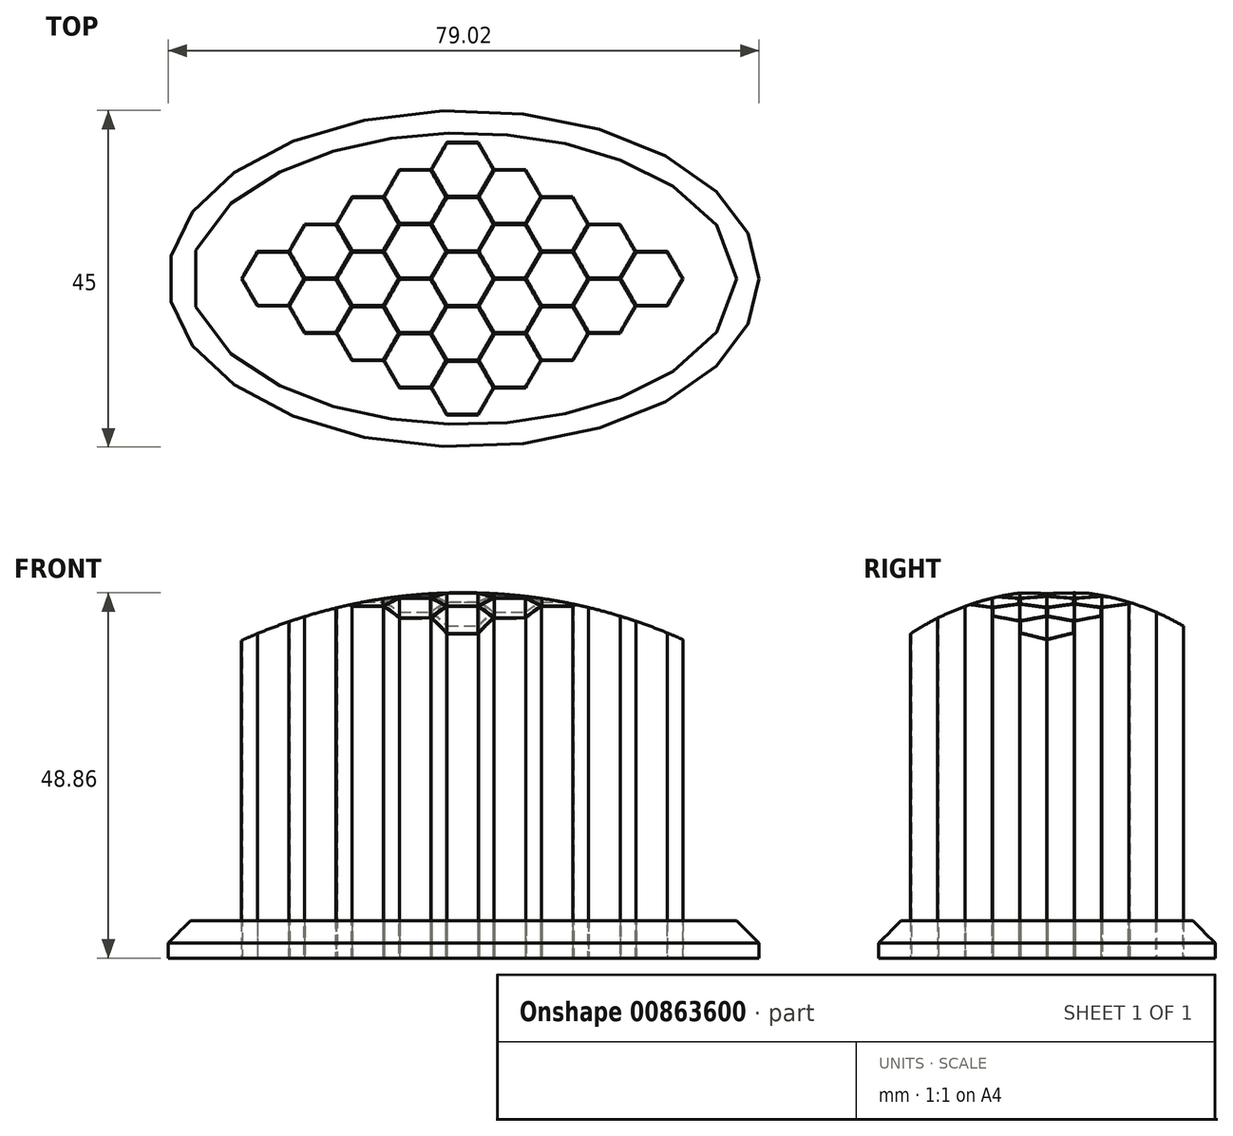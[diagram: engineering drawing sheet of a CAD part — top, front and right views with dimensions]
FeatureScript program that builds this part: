
annotation { "Feature Type Name" : "Feature", "Feature Type Description" : "" }
export const myFeature = defineFeature(function(context is Context, id is Id, definition is map)
    precondition{}
    {
        {
            var Q0;
            Q0=qCreatedBy(makeId("Top.planeOp"),FACE);
            var sketch = newSketch(context, id + "F0", { "sketchPlane" : qUnion([Q0])});
            skCircle(sketch, "E0.cCircle", {"center": v(0, 0) * mm, "radius": 3.55 * mm, "construction": true});
            skLineSegment(sketch, "E0.0", {"start": v(4.1, 0) * mm, "end": v(2.05, -3.55) * mm});
            skLineSegment(sketch, "E0.1", {"start": v(2.05, -3.55) * mm, "end": v(-2.05, -3.55) * mm});
            skLineSegment(sketch, "E0.2", {"start": v(-2.05, -3.55) * mm, "end": v(-4.1, 0) * mm});
            skLineSegment(sketch, "E0.3", {"start": v(-4.1, 0) * mm, "end": v(-2.05, 3.55) * mm});
            skLineSegment(sketch, "E0.4", {"start": v(-2.05, 3.55) * mm, "end": v(2.05, 3.55) * mm});
            skLineSegment(sketch, "E0.5", {"start": v(2.05, 3.55) * mm, "end": v(4.1, 0) * mm});
            skPoint(sketch, "E0.0.midPoint", {"position": v(3.07, -1.78) * mm});
            skCircle(sketch, "E1.cCircle", {"center": v(0, 0) * mm, "radius": 3.65 * mm, "construction": true});
            skLineSegment(sketch, "E1.0", {"start": v(4.21, 0) * mm, "end": v(2.1, -3.65) * mm});
            skLineSegment(sketch, "E1.1", {"start": v(2.1, -3.65) * mm, "end": v(-2.1, -3.65) * mm});
            skLineSegment(sketch, "E1.2", {"start": v(-2.1, -3.65) * mm, "end": v(-4.21, 0) * mm});
            skLineSegment(sketch, "E1.3", {"start": v(-4.21, 0) * mm, "end": v(-2.1, 3.65) * mm});
            skLineSegment(sketch, "E1.4", {"start": v(-2.1, 3.65) * mm, "end": v(2.1, 3.65) * mm});
            skLineSegment(sketch, "E1.5", {"start": v(2.1, 3.65) * mm, "end": v(4.21, 0) * mm});
            skPoint(sketch, "E1.0.midPoint", {"position": v(3.16, -1.82) * mm});
            skSolve(sketch);
        }
        {
            var Q0;
            Q0 = qSketchRegion(id + "F0", true);
            extrude(context, id + "F1", {"entities" : qUnion([Q0]), "depth" : 50 * mm, "offsetDistance" : 25 * mm});
        }
        {
            var Q0;
            Q0=makeQuery(id+"F1.opExtrude","SWEPT_BODY",BODY,{"disambiguationData":[OSD([sQuery(id+"F0.wireOp",EDGE,"E0.0"),sQuery(id+"F0.wireOp",EDGE,"E0.1"),sQuery(id+"F0.wireOp",EDGE,"E0.2"),sQuery(id+"F0.wireOp",EDGE,"E0.3"),sQuery(id+"F0.wireOp",EDGE,"E0.4"),sQuery(id+"F0.wireOp",EDGE,"E0.5"),sQuery(id+"F0.wireOp",EDGE,"E1.0"),sQuery(id+"F0.wireOp",EDGE,"E1.1"),sQuery(id+"F0.wireOp",EDGE,"E1.2"),sQuery(id+"F0.wireOp",EDGE,"E1.3"),sQuery(id+"F0.wireOp",EDGE,"E1.4"),sQuery(id+"F0.wireOp",EDGE,"E1.5")])]});
            transform(context, id + "F2", {"entities" : qUnion([Q0]), "transformType" : TransformType.TRANSLATION_3D, "dx" : 6.32 * mm, "dy" : -3.65 * mm, "dz" : 0 * mm, "makeCopy" : true});
        }
        {
            var Q0;
            Q0=makeQuery(id+"F2.opPattern","COPY",BODY,{"derivedFrom":makeQuery(id+"F1.opExtrude","SWEPT_BODY",BODY,{"disambiguationData":[OSD([sQuery(id+"F0.wireOp",EDGE,"E0.0"),sQuery(id+"F0.wireOp",EDGE,"E0.1"),sQuery(id+"F0.wireOp",EDGE,"E0.2"),sQuery(id+"F0.wireOp",EDGE,"E0.3"),sQuery(id+"F0.wireOp",EDGE,"E0.4"),sQuery(id+"F0.wireOp",EDGE,"E0.5"),sQuery(id+"F0.wireOp",EDGE,"E1.0"),sQuery(id+"F0.wireOp",EDGE,"E1.1"),sQuery(id+"F0.wireOp",EDGE,"E1.2"),sQuery(id+"F0.wireOp",EDGE,"E1.3"),sQuery(id+"F0.wireOp",EDGE,"E1.4"),sQuery(id+"F0.wireOp",EDGE,"E1.5")])]}),"instanceName":"1"});
            transform(context, id + "F3", {"entities" : qUnion([Q0]), "transformType" : TransformType.TRANSLATION_3D, "dx" : 0 * mm, "dy" : 7.3 * mm, "dz" : 0 * mm, "makeCopy" : true});
        }
        {
            var Q0;
            Q0=makeQuery(id+"F1.opExtrude","SWEPT_BODY",BODY,{"disambiguationData":[OSD([sQuery(id+"F0.wireOp",EDGE,"E0.0"),sQuery(id+"F0.wireOp",EDGE,"E0.1"),sQuery(id+"F0.wireOp",EDGE,"E0.2"),sQuery(id+"F0.wireOp",EDGE,"E0.3"),sQuery(id+"F0.wireOp",EDGE,"E0.4"),sQuery(id+"F0.wireOp",EDGE,"E0.5"),sQuery(id+"F0.wireOp",EDGE,"E1.0"),sQuery(id+"F0.wireOp",EDGE,"E1.1"),sQuery(id+"F0.wireOp",EDGE,"E1.2"),sQuery(id+"F0.wireOp",EDGE,"E1.3"),sQuery(id+"F0.wireOp",EDGE,"E1.4"),sQuery(id+"F0.wireOp",EDGE,"E1.5")])]});
            transform(context, id + "F4", {"entities" : qUnion([Q0]), "transformType" : TransformType.TRANSLATION_3D, "dx" : 12.67 * mm, "dy" : 0 * mm, "dz" : 0 * mm, "makeCopy" : true});
        }
        {
            var Q0;
            Q0=makeQuery(id+"F2.opPattern","COPY",BODY,{"derivedFrom":makeQuery(id+"F1.opExtrude","SWEPT_BODY",BODY,{"disambiguationData":[OSD([sQuery(id+"F0.wireOp",EDGE,"E0.0"),sQuery(id+"F0.wireOp",EDGE,"E0.1"),sQuery(id+"F0.wireOp",EDGE,"E0.2"),sQuery(id+"F0.wireOp",EDGE,"E0.3"),sQuery(id+"F0.wireOp",EDGE,"E0.4"),sQuery(id+"F0.wireOp",EDGE,"E0.5"),sQuery(id+"F0.wireOp",EDGE,"E1.0"),sQuery(id+"F0.wireOp",EDGE,"E1.1"),sQuery(id+"F0.wireOp",EDGE,"E1.2"),sQuery(id+"F0.wireOp",EDGE,"E1.3"),sQuery(id+"F0.wireOp",EDGE,"E1.4"),sQuery(id+"F0.wireOp",EDGE,"E1.5")])]}),"instanceName":"1"});
            transform(context, id + "F5", {"entities" : qUnion([Q0]), "transformType" : TransformType.TRANSLATION_3D, "dx" : 12.68 * mm, "dy" : 0 * mm, "dz" : 0 * mm, "makeCopy" : true});
        }
        {
            var Q0;
            Q0=makeQuery(id+"F3.opPattern","COPY",BODY,{"derivedFrom":makeQuery(id+"F2.opPattern","COPY",BODY,{"derivedFrom":makeQuery(id+"F1.opExtrude","SWEPT_BODY",BODY,{"disambiguationData":[OSD([sQuery(id+"F0.wireOp",EDGE,"E0.0"),sQuery(id+"F0.wireOp",EDGE,"E0.1"),sQuery(id+"F0.wireOp",EDGE,"E0.2"),sQuery(id+"F0.wireOp",EDGE,"E0.3"),sQuery(id+"F0.wireOp",EDGE,"E0.4"),sQuery(id+"F0.wireOp",EDGE,"E0.5"),sQuery(id+"F0.wireOp",EDGE,"E1.0"),sQuery(id+"F0.wireOp",EDGE,"E1.1"),sQuery(id+"F0.wireOp",EDGE,"E1.2"),sQuery(id+"F0.wireOp",EDGE,"E1.3"),sQuery(id+"F0.wireOp",EDGE,"E1.4"),sQuery(id+"F0.wireOp",EDGE,"E1.5")])]}),"instanceName":"1"}),"instanceName":"1"});
            transform(context, id + "F6", {"entities" : qUnion([Q0]), "transformType" : TransformType.TRANSLATION_3D, "dx" : 12.7 * mm, "dy" : 0 * mm, "dz" : 0 * mm, "makeCopy" : true});
        }
        {
            var Q0;
            Q0=makeQuery(id+"F1.opExtrude","SWEPT_BODY",BODY,{"disambiguationData":[OSD([sQuery(id+"F0.wireOp",EDGE,"E0.0"),sQuery(id+"F0.wireOp",EDGE,"E0.1"),sQuery(id+"F0.wireOp",EDGE,"E0.2"),sQuery(id+"F0.wireOp",EDGE,"E0.3"),sQuery(id+"F0.wireOp",EDGE,"E0.4"),sQuery(id+"F0.wireOp",EDGE,"E0.5"),sQuery(id+"F0.wireOp",EDGE,"E1.0"),sQuery(id+"F0.wireOp",EDGE,"E1.1"),sQuery(id+"F0.wireOp",EDGE,"E1.2"),sQuery(id+"F0.wireOp",EDGE,"E1.3"),sQuery(id+"F0.wireOp",EDGE,"E1.4"),sQuery(id+"F0.wireOp",EDGE,"E1.5")])]});
            transform(context, id + "F7", {"entities" : qUnion([Q0]), "transformType" : TransformType.TRANSLATION_3D, "dx" : 25.33 * mm, "dy" : 0 * mm, "dz" : 0 * mm, "makeCopy" : true});
        }
        {
            var Q0;
            Q0=makeQuery(id+"F2.opPattern","COPY",BODY,{"derivedFrom":makeQuery(id+"F1.opExtrude","SWEPT_BODY",BODY,{"disambiguationData":[OSD([sQuery(id+"F0.wireOp",EDGE,"E0.0"),sQuery(id+"F0.wireOp",EDGE,"E0.1"),sQuery(id+"F0.wireOp",EDGE,"E0.2"),sQuery(id+"F0.wireOp",EDGE,"E0.3"),sQuery(id+"F0.wireOp",EDGE,"E0.4"),sQuery(id+"F0.wireOp",EDGE,"E0.5"),sQuery(id+"F0.wireOp",EDGE,"E1.0"),sQuery(id+"F0.wireOp",EDGE,"E1.1"),sQuery(id+"F0.wireOp",EDGE,"E1.2"),sQuery(id+"F0.wireOp",EDGE,"E1.3"),sQuery(id+"F0.wireOp",EDGE,"E1.4"),sQuery(id+"F0.wireOp",EDGE,"E1.5")])]}),"instanceName":"1"});
            transform(context, id + "F8", {"entities" : qUnion([Q0]), "transformType" : TransformType.TRANSLATION_3D, "dx" : 25.34 * mm, "dy" : 0 * mm, "dz" : 0 * mm, "makeCopy" : true});
        }
        {
            var Q0;
            Q0=makeQuery(id+"F3.opPattern","COPY",BODY,{"derivedFrom":makeQuery(id+"F2.opPattern","COPY",BODY,{"derivedFrom":makeQuery(id+"F1.opExtrude","SWEPT_BODY",BODY,{"disambiguationData":[OSD([sQuery(id+"F0.wireOp",EDGE,"E0.0"),sQuery(id+"F0.wireOp",EDGE,"E0.1"),sQuery(id+"F0.wireOp",EDGE,"E0.2"),sQuery(id+"F0.wireOp",EDGE,"E0.3"),sQuery(id+"F0.wireOp",EDGE,"E0.4"),sQuery(id+"F0.wireOp",EDGE,"E0.5"),sQuery(id+"F0.wireOp",EDGE,"E1.0"),sQuery(id+"F0.wireOp",EDGE,"E1.1"),sQuery(id+"F0.wireOp",EDGE,"E1.2"),sQuery(id+"F0.wireOp",EDGE,"E1.3"),sQuery(id+"F0.wireOp",EDGE,"E1.4"),sQuery(id+"F0.wireOp",EDGE,"E1.5")])]}),"instanceName":"1"}),"instanceName":"1"});
            transform(context, id + "F9", {"entities" : qUnion([Q0]), "transformType" : TransformType.TRANSLATION_3D, "dx" : 25.34 * mm, "dy" : 0 * mm, "dz" : 0 * mm, "makeCopy" : true});
        }
        {
            var Q0;
            Q0=makeQuery(id+"F1.opExtrude","SWEPT_BODY",BODY,{"disambiguationData":[OSD([sQuery(id+"F0.wireOp",EDGE,"E0.0"),sQuery(id+"F0.wireOp",EDGE,"E0.1"),sQuery(id+"F0.wireOp",EDGE,"E0.2"),sQuery(id+"F0.wireOp",EDGE,"E0.3"),sQuery(id+"F0.wireOp",EDGE,"E0.4"),sQuery(id+"F0.wireOp",EDGE,"E0.5"),sQuery(id+"F0.wireOp",EDGE,"E1.0"),sQuery(id+"F0.wireOp",EDGE,"E1.1"),sQuery(id+"F0.wireOp",EDGE,"E1.2"),sQuery(id+"F0.wireOp",EDGE,"E1.3"),sQuery(id+"F0.wireOp",EDGE,"E1.4"),sQuery(id+"F0.wireOp",EDGE,"E1.5")])]});
            transform(context, id + "F10", {"entities" : qUnion([Q0]), "transformType" : TransformType.TRANSLATION_3D, "dx" : 37.98 * mm, "dy" : 0 * mm, "dz" : 0 * mm, "makeCopy" : true});
        }
        {
            var Q0;
            Q0=makeQuery(id+"F2.opPattern","COPY",BODY,{"derivedFrom":makeQuery(id+"F1.opExtrude","SWEPT_BODY",BODY,{"disambiguationData":[OSD([sQuery(id+"F0.wireOp",EDGE,"E0.0"),sQuery(id+"F0.wireOp",EDGE,"E0.1"),sQuery(id+"F0.wireOp",EDGE,"E0.2"),sQuery(id+"F0.wireOp",EDGE,"E0.3"),sQuery(id+"F0.wireOp",EDGE,"E0.4"),sQuery(id+"F0.wireOp",EDGE,"E0.5"),sQuery(id+"F0.wireOp",EDGE,"E1.0"),sQuery(id+"F0.wireOp",EDGE,"E1.1"),sQuery(id+"F0.wireOp",EDGE,"E1.2"),sQuery(id+"F0.wireOp",EDGE,"E1.3"),sQuery(id+"F0.wireOp",EDGE,"E1.4"),sQuery(id+"F0.wireOp",EDGE,"E1.5")])]}),"instanceName":"1"});
            transform(context, id + "F11", {"entities" : qUnion([Q0]), "transformType" : TransformType.TRANSLATION_3D, "dx" : 38 * mm, "dy" : 0 * mm, "dz" : 0 * mm, "makeCopy" : true});
        }
        {
            var Q0;
            Q0=makeQuery(id+"F3.opPattern","COPY",BODY,{"derivedFrom":makeQuery(id+"F2.opPattern","COPY",BODY,{"derivedFrom":makeQuery(id+"F1.opExtrude","SWEPT_BODY",BODY,{"disambiguationData":[OSD([sQuery(id+"F0.wireOp",EDGE,"E0.0"),sQuery(id+"F0.wireOp",EDGE,"E0.1"),sQuery(id+"F0.wireOp",EDGE,"E0.2"),sQuery(id+"F0.wireOp",EDGE,"E0.3"),sQuery(id+"F0.wireOp",EDGE,"E0.4"),sQuery(id+"F0.wireOp",EDGE,"E0.5"),sQuery(id+"F0.wireOp",EDGE,"E1.0"),sQuery(id+"F0.wireOp",EDGE,"E1.1"),sQuery(id+"F0.wireOp",EDGE,"E1.2"),sQuery(id+"F0.wireOp",EDGE,"E1.3"),sQuery(id+"F0.wireOp",EDGE,"E1.4"),sQuery(id+"F0.wireOp",EDGE,"E1.5")])]}),"instanceName":"1"}),"instanceName":"1"});
            transform(context, id + "F12", {"entities" : qUnion([Q0]), "transformType" : TransformType.TRANSLATION_3D, "dx" : 37.98 * mm, "dy" : 0 * mm, "dz" : 0 * mm, "makeCopy" : true});
        }
        {
            var Q0;
            Q0=makeQuery(id+"F1.opExtrude","SWEPT_BODY",BODY,{"disambiguationData":[OSD([sQuery(id+"F0.wireOp",EDGE,"E0.0"),sQuery(id+"F0.wireOp",EDGE,"E0.1"),sQuery(id+"F0.wireOp",EDGE,"E0.2"),sQuery(id+"F0.wireOp",EDGE,"E0.3"),sQuery(id+"F0.wireOp",EDGE,"E0.4"),sQuery(id+"F0.wireOp",EDGE,"E0.5"),sQuery(id+"F0.wireOp",EDGE,"E1.0"),sQuery(id+"F0.wireOp",EDGE,"E1.1"),sQuery(id+"F0.wireOp",EDGE,"E1.2"),sQuery(id+"F0.wireOp",EDGE,"E1.3"),sQuery(id+"F0.wireOp",EDGE,"E1.4"),sQuery(id+"F0.wireOp",EDGE,"E1.5")])]});
            transform(context, id + "F13", {"entities" : qUnion([Q0]), "transformType" : TransformType.TRANSLATION_3D, "dx" : 50.63 * mm, "dy" : 0 * mm, "dz" : 0 * mm, "makeCopy" : true});
        }
        {
            var Q0;
            Q0=makeQuery(id+"F1.opExtrude","SWEPT_BODY",BODY,{"disambiguationData":[OSD([sQuery(id+"F0.wireOp",EDGE,"E0.0"),sQuery(id+"F0.wireOp",EDGE,"E0.1"),sQuery(id+"F0.wireOp",EDGE,"E0.2"),sQuery(id+"F0.wireOp",EDGE,"E0.3"),sQuery(id+"F0.wireOp",EDGE,"E0.4"),sQuery(id+"F0.wireOp",EDGE,"E0.5"),sQuery(id+"F0.wireOp",EDGE,"E1.0"),sQuery(id+"F0.wireOp",EDGE,"E1.1"),sQuery(id+"F0.wireOp",EDGE,"E1.2"),sQuery(id+"F0.wireOp",EDGE,"E1.3"),sQuery(id+"F0.wireOp",EDGE,"E1.4"),sQuery(id+"F0.wireOp",EDGE,"E1.5")])]});
            transform(context, id + "F14", {"entities" : qUnion([Q0]), "transformType" : TransformType.TRANSLATION_3D, "dx" : 12.66 * mm, "dy" : 7.3 * mm, "dz" : 0 * mm, "makeCopy" : true});
        }
        {
            var Q0;
            Q0=makeQuery(id+"F14.opPattern","COPY",BODY,{"derivedFrom":makeQuery(id+"F1.opExtrude","SWEPT_BODY",BODY,{"disambiguationData":[OSD([sQuery(id+"F0.wireOp",EDGE,"E0.0"),sQuery(id+"F0.wireOp",EDGE,"E0.1"),sQuery(id+"F0.wireOp",EDGE,"E0.2"),sQuery(id+"F0.wireOp",EDGE,"E0.3"),sQuery(id+"F0.wireOp",EDGE,"E0.4"),sQuery(id+"F0.wireOp",EDGE,"E0.5"),sQuery(id+"F0.wireOp",EDGE,"E1.0"),sQuery(id+"F0.wireOp",EDGE,"E1.1"),sQuery(id+"F0.wireOp",EDGE,"E1.2"),sQuery(id+"F0.wireOp",EDGE,"E1.3"),sQuery(id+"F0.wireOp",EDGE,"E1.4"),sQuery(id+"F0.wireOp",EDGE,"E1.5")])]}),"instanceName":"1"});
            transform(context, id + "F15", {"entities" : qUnion([Q0]), "transformType" : TransformType.TRANSLATION_3D, "dx" : 12.68 * mm, "dy" : 0 * mm, "dz" : 0 * mm, "makeCopy" : true});
        }
        {
            var Q0;
            Q0=makeQuery(id+"F14.opPattern","COPY",BODY,{"derivedFrom":makeQuery(id+"F1.opExtrude","SWEPT_BODY",BODY,{"disambiguationData":[OSD([sQuery(id+"F0.wireOp",EDGE,"E0.0"),sQuery(id+"F0.wireOp",EDGE,"E0.1"),sQuery(id+"F0.wireOp",EDGE,"E0.2"),sQuery(id+"F0.wireOp",EDGE,"E0.3"),sQuery(id+"F0.wireOp",EDGE,"E0.4"),sQuery(id+"F0.wireOp",EDGE,"E0.5"),sQuery(id+"F0.wireOp",EDGE,"E1.0"),sQuery(id+"F0.wireOp",EDGE,"E1.1"),sQuery(id+"F0.wireOp",EDGE,"E1.2"),sQuery(id+"F0.wireOp",EDGE,"E1.3"),sQuery(id+"F0.wireOp",EDGE,"E1.4"),sQuery(id+"F0.wireOp",EDGE,"E1.5")])]}),"instanceName":"1"});
            transform(context, id + "F16", {"entities" : qUnion([Q0]), "transformType" : TransformType.TRANSLATION_3D, "dx" : 25.3 * mm, "dy" : 0 * mm, "dz" : 0 * mm, "makeCopy" : true});
        }
        {
            var Q0;
            Q0=makeQuery(id+"F14.opPattern","COPY",BODY,{"derivedFrom":makeQuery(id+"F1.opExtrude","SWEPT_BODY",BODY,{"disambiguationData":[OSD([sQuery(id+"F0.wireOp",EDGE,"E0.0"),sQuery(id+"F0.wireOp",EDGE,"E0.1"),sQuery(id+"F0.wireOp",EDGE,"E0.2"),sQuery(id+"F0.wireOp",EDGE,"E0.3"),sQuery(id+"F0.wireOp",EDGE,"E0.4"),sQuery(id+"F0.wireOp",EDGE,"E0.5"),sQuery(id+"F0.wireOp",EDGE,"E1.0"),sQuery(id+"F0.wireOp",EDGE,"E1.1"),sQuery(id+"F0.wireOp",EDGE,"E1.2"),sQuery(id+"F0.wireOp",EDGE,"E1.3"),sQuery(id+"F0.wireOp",EDGE,"E1.4"),sQuery(id+"F0.wireOp",EDGE,"E1.5")])]}),"instanceName":"1"});
            transform(context, id + "F17", {"entities" : qUnion([Q0]), "transformType" : TransformType.TRANSLATION_3D, "dx" : 0 * mm, "dy" : -14.62 * mm, "dz" : 0 * mm, "makeCopy" : true});
        }
        {
            var Q0;
            Q0=makeQuery(id+"F17.opPattern","COPY",BODY,{"derivedFrom":makeQuery(id+"F14.opPattern","COPY",BODY,{"derivedFrom":makeQuery(id+"F1.opExtrude","SWEPT_BODY",BODY,{"disambiguationData":[OSD([sQuery(id+"F0.wireOp",EDGE,"E0.0"),sQuery(id+"F0.wireOp",EDGE,"E0.1"),sQuery(id+"F0.wireOp",EDGE,"E0.2"),sQuery(id+"F0.wireOp",EDGE,"E0.3"),sQuery(id+"F0.wireOp",EDGE,"E0.4"),sQuery(id+"F0.wireOp",EDGE,"E0.5"),sQuery(id+"F0.wireOp",EDGE,"E1.0"),sQuery(id+"F0.wireOp",EDGE,"E1.1"),sQuery(id+"F0.wireOp",EDGE,"E1.2"),sQuery(id+"F0.wireOp",EDGE,"E1.3"),sQuery(id+"F0.wireOp",EDGE,"E1.4"),sQuery(id+"F0.wireOp",EDGE,"E1.5")])]}),"instanceName":"1"}),"instanceName":"1"});
            transform(context, id + "F18", {"entities" : qUnion([Q0]), "transformType" : TransformType.TRANSLATION_3D, "dx" : 12.67 * mm, "dy" : 0 * mm, "dz" : 0 * mm, "makeCopy" : true});
        }
        {
            var Q0;
            Q0=makeQuery(id+"F18.opPattern","COPY",BODY,{"derivedFrom":makeQuery(id+"F17.opPattern","COPY",BODY,{"derivedFrom":makeQuery(id+"F14.opPattern","COPY",BODY,{"derivedFrom":makeQuery(id+"F1.opExtrude","SWEPT_BODY",BODY,{"disambiguationData":[OSD([sQuery(id+"F0.wireOp",EDGE,"E0.0"),sQuery(id+"F0.wireOp",EDGE,"E0.1"),sQuery(id+"F0.wireOp",EDGE,"E0.2"),sQuery(id+"F0.wireOp",EDGE,"E0.3"),sQuery(id+"F0.wireOp",EDGE,"E0.4"),sQuery(id+"F0.wireOp",EDGE,"E0.5"),sQuery(id+"F0.wireOp",EDGE,"E1.0"),sQuery(id+"F0.wireOp",EDGE,"E1.1"),sQuery(id+"F0.wireOp",EDGE,"E1.2"),sQuery(id+"F0.wireOp",EDGE,"E1.3"),sQuery(id+"F0.wireOp",EDGE,"E1.4"),sQuery(id+"F0.wireOp",EDGE,"E1.5")])]}),"instanceName":"1"}),"instanceName":"1"}),"instanceName":"1"});
            transform(context, id + "F19", {"entities" : qUnion([Q0]), "transformType" : TransformType.TRANSLATION_3D, "dx" : 12.66 * mm, "dy" : 0 * mm, "dz" : 0 * mm, "makeCopy" : true});
        }
        {
            var Q0;
            Q0=makeQuery(id+"F1.opExtrude","SWEPT_BODY",BODY,{"disambiguationData":[OSD([sQuery(id+"F0.wireOp",EDGE,"E0.0"),sQuery(id+"F0.wireOp",EDGE,"E0.1"),sQuery(id+"F0.wireOp",EDGE,"E0.2"),sQuery(id+"F0.wireOp",EDGE,"E0.3"),sQuery(id+"F0.wireOp",EDGE,"E0.4"),sQuery(id+"F0.wireOp",EDGE,"E0.5"),sQuery(id+"F0.wireOp",EDGE,"E1.0"),sQuery(id+"F0.wireOp",EDGE,"E1.1"),sQuery(id+"F0.wireOp",EDGE,"E1.2"),sQuery(id+"F0.wireOp",EDGE,"E1.3"),sQuery(id+"F0.wireOp",EDGE,"E1.4"),sQuery(id+"F0.wireOp",EDGE,"E1.5")])]});
            transform(context, id + "F20", {"entities" : qUnion([Q0]), "transformType" : TransformType.TRANSLATION_3D, "dx" : 19 * mm, "dy" : 10.96 * mm, "dz" : 0 * mm, "makeCopy" : true});
        }
        {
            var Q0;
            Q0=makeQuery(id+"F20.opPattern","COPY",BODY,{"derivedFrom":makeQuery(id+"F1.opExtrude","SWEPT_BODY",BODY,{"disambiguationData":[OSD([sQuery(id+"F0.wireOp",EDGE,"E0.0"),sQuery(id+"F0.wireOp",EDGE,"E0.1"),sQuery(id+"F0.wireOp",EDGE,"E0.2"),sQuery(id+"F0.wireOp",EDGE,"E0.3"),sQuery(id+"F0.wireOp",EDGE,"E0.4"),sQuery(id+"F0.wireOp",EDGE,"E0.5"),sQuery(id+"F0.wireOp",EDGE,"E1.0"),sQuery(id+"F0.wireOp",EDGE,"E1.1"),sQuery(id+"F0.wireOp",EDGE,"E1.2"),sQuery(id+"F0.wireOp",EDGE,"E1.3"),sQuery(id+"F0.wireOp",EDGE,"E1.4"),sQuery(id+"F0.wireOp",EDGE,"E1.5")])]}),"instanceName":"1"});
            transform(context, id + "F21", {"entities" : qUnion([Q0]), "transformType" : TransformType.TRANSLATION_3D, "dx" : 12.67 * mm, "dy" : 0 * mm, "dz" : 0 * mm, "makeCopy" : true});
        }
        {
            var Q0;
            Q0=makeQuery(id+"F21.opPattern","COPY",BODY,{"derivedFrom":makeQuery(id+"F20.opPattern","COPY",BODY,{"derivedFrom":makeQuery(id+"F1.opExtrude","SWEPT_BODY",BODY,{"disambiguationData":[OSD([sQuery(id+"F0.wireOp",EDGE,"E0.0"),sQuery(id+"F0.wireOp",EDGE,"E0.1"),sQuery(id+"F0.wireOp",EDGE,"E0.2"),sQuery(id+"F0.wireOp",EDGE,"E0.3"),sQuery(id+"F0.wireOp",EDGE,"E0.4"),sQuery(id+"F0.wireOp",EDGE,"E0.5"),sQuery(id+"F0.wireOp",EDGE,"E1.0"),sQuery(id+"F0.wireOp",EDGE,"E1.1"),sQuery(id+"F0.wireOp",EDGE,"E1.2"),sQuery(id+"F0.wireOp",EDGE,"E1.3"),sQuery(id+"F0.wireOp",EDGE,"E1.4"),sQuery(id+"F0.wireOp",EDGE,"E1.5")])]}),"instanceName":"1"}),"instanceName":"1"});
            transform(context, id + "F22", {"entities" : qUnion([Q0]), "transformType" : TransformType.TRANSLATION_3D, "dx" : 0 * mm, "dy" : -21.91 * mm, "dz" : 0 * mm, "makeCopy" : true});
        }
        {
            var Q0;
            Q0=makeQuery(id+"F22.opPattern","COPY",BODY,{"derivedFrom":makeQuery(id+"F21.opPattern","COPY",BODY,{"derivedFrom":makeQuery(id+"F20.opPattern","COPY",BODY,{"derivedFrom":makeQuery(id+"F1.opExtrude","SWEPT_BODY",BODY,{"disambiguationData":[OSD([sQuery(id+"F0.wireOp",EDGE,"E0.0"),sQuery(id+"F0.wireOp",EDGE,"E0.1"),sQuery(id+"F0.wireOp",EDGE,"E0.2"),sQuery(id+"F0.wireOp",EDGE,"E0.3"),sQuery(id+"F0.wireOp",EDGE,"E0.4"),sQuery(id+"F0.wireOp",EDGE,"E0.5"),sQuery(id+"F0.wireOp",EDGE,"E1.0"),sQuery(id+"F0.wireOp",EDGE,"E1.1"),sQuery(id+"F0.wireOp",EDGE,"E1.2"),sQuery(id+"F0.wireOp",EDGE,"E1.3"),sQuery(id+"F0.wireOp",EDGE,"E1.4"),sQuery(id+"F0.wireOp",EDGE,"E1.5")])]}),"instanceName":"1"}),"instanceName":"1"}),"instanceName":"1"});
            transform(context, id + "F23", {"entities" : qUnion([Q0]), "transformType" : TransformType.TRANSLATION_3D, "dx" : -12.68 * mm, "dy" : 0 * mm, "dz" : 0 * mm, "makeCopy" : true});
        }
        {
            var Q0;
            Q0=makeQuery(id+"F15.opPattern","COPY",BODY,{"derivedFrom":makeQuery(id+"F14.opPattern","COPY",BODY,{"derivedFrom":makeQuery(id+"F1.opExtrude","SWEPT_BODY",BODY,{"disambiguationData":[OSD([sQuery(id+"F0.wireOp",EDGE,"E0.0"),sQuery(id+"F0.wireOp",EDGE,"E0.1"),sQuery(id+"F0.wireOp",EDGE,"E0.2"),sQuery(id+"F0.wireOp",EDGE,"E0.3"),sQuery(id+"F0.wireOp",EDGE,"E0.4"),sQuery(id+"F0.wireOp",EDGE,"E0.5"),sQuery(id+"F0.wireOp",EDGE,"E1.0"),sQuery(id+"F0.wireOp",EDGE,"E1.1"),sQuery(id+"F0.wireOp",EDGE,"E1.2"),sQuery(id+"F0.wireOp",EDGE,"E1.3"),sQuery(id+"F0.wireOp",EDGE,"E1.4"),sQuery(id+"F0.wireOp",EDGE,"E1.5")])]}),"instanceName":"1"}),"instanceName":"1"});
            transform(context, id + "F24", {"entities" : qUnion([Q0]), "transformType" : TransformType.TRANSLATION_3D, "dx" : 0 * mm, "dy" : 7.3 * mm, "dz" : 0 * mm, "makeCopy" : true});
        }
        {
            var Q0;
            Q0=makeQuery(id+"F24.opPattern","COPY",BODY,{"derivedFrom":makeQuery(id+"F15.opPattern","COPY",BODY,{"derivedFrom":makeQuery(id+"F14.opPattern","COPY",BODY,{"derivedFrom":makeQuery(id+"F1.opExtrude","SWEPT_BODY",BODY,{"disambiguationData":[OSD([sQuery(id+"F0.wireOp",EDGE,"E0.0"),sQuery(id+"F0.wireOp",EDGE,"E0.1"),sQuery(id+"F0.wireOp",EDGE,"E0.2"),sQuery(id+"F0.wireOp",EDGE,"E0.3"),sQuery(id+"F0.wireOp",EDGE,"E0.4"),sQuery(id+"F0.wireOp",EDGE,"E0.5"),sQuery(id+"F0.wireOp",EDGE,"E1.0"),sQuery(id+"F0.wireOp",EDGE,"E1.1"),sQuery(id+"F0.wireOp",EDGE,"E1.2"),sQuery(id+"F0.wireOp",EDGE,"E1.3"),sQuery(id+"F0.wireOp",EDGE,"E1.4"),sQuery(id+"F0.wireOp",EDGE,"E1.5")])]}),"instanceName":"1"}),"instanceName":"1"}),"instanceName":"1"});
            transform(context, id + "F25", {"entities" : qUnion([Q0]), "transformType" : TransformType.TRANSLATION_3D, "dx" : 0 * mm, "dy" : -29.2 * mm, "dz" : 0 * mm, "makeCopy" : true});
        }
        {
            var Q0;
            Q0=qCreatedBy(makeId("Top.planeOp"),FACE);
            var sketch = newSketch(context, id + "F26", { "sketchPlane" : qUnion([Q0])});
            skEllipse(sketch, "E2", {"center": v(25.48, 0) * mm, "majorRadius": 39.51 * mm, "minorRadius": 22.5 * mm, "majorAxis": v(1, 0)});
            skSolve(sketch);
        }
        {
            var Q0;
            Q0 = qSketchRegion(id + "F26", true);
            extrude(context, id + "F27", {"entities" : qUnion([Q0]), "depth" : 5 * mm, "offsetDistance" : 25 * mm});
        }
        {
            var Q0;
            Q0=makeQuery(id+"F27.opExtrude","CAP_FACE",FACE,{"disambiguationData":[OSD([sQuery(id+"F26.wireOp",EDGE,"E2")])],"isStart":false});
            chamfer(context, id + "F28", {"entities" : qUnion([Q0]), "width" : 3 * mm, "tangentPropagation" : true});
        }
        {
            var Q0;
            Q0=qCreatedBy(makeId("Right.planeOp"),FACE);
            var sketch = newSketch(context, id + "F29", { "sketchPlane" : qUnion([Q0])});
            skArc(sketch, "E3", {"start": v(22.27, 41.66) * mm, "mid": v(-0.1, 49.1) * mm, "end": v(-22.03, 40.47) * mm});
            skLineSegment(sketch, "E4", {"start": v(22.27, 41.66) * mm, "end": v(22.27, 53.4) * mm});
            skLineSegment(sketch, "E5", {"start": v(22.27, 53.4) * mm, "end": v(-22.03, 53.4) * mm});
            skLineSegment(sketch, "E6", {"start": v(-22.03, 53.4) * mm, "end": v(-22.03, 40.47) * mm});
            skSolve(sketch);
        }
        {
            var Q0;
            Q0 = qSketchRegion(id + "F29", true);
            extrude(context, id + "F30", {"entities" : qUnion([Q0]), "operationType" : NewBodyOperationType.REMOVE, "depth" : 64.8 * mm, "offsetDistance" : 25 * mm, "hasSecondDirection" : true, "secondDirectionOppositeDirection" : true, "secondDirectionDepth" : 25 * mm});
        }
        {
            var Q0;
            Q0=qCreatedBy(makeId("Front.planeOp"),FACE);
            var sketch = newSketch(context, id + "F31", { "sketchPlane" : qUnion([Q0])});
            skArc(sketch, "E7", {"start": v(56.8, 41.67) * mm, "mid": v(25.15, 48.86) * mm, "end": v(-6.45, 41.42) * mm});
            skLineSegment(sketch, "E8", {"start": v(-6.45, 41.42) * mm, "end": v(-6.45, 54.81) * mm});
            skLineSegment(sketch, "E9", {"start": v(-6.45, 54.81) * mm, "end": v(56.8, 54.81) * mm});
            skLineSegment(sketch, "E10", {"start": v(56.8, 54.81) * mm, "end": v(56.8, 41.67) * mm});
            skSolve(sketch);
        }
        {
            var Q0;
            Q0 = qSketchRegion(id + "F31", true);
            extrude(context, id + "F32", {"entities" : qUnion([Q0]), "operationType" : NewBodyOperationType.REMOVE, "oppositeDirection" : true, "depth" : 25 * mm, "offsetDistance" : 25 * mm, "hasSecondDirection" : true, "secondDirectionOppositeDirection" : false, "secondDirectionDepth" : 25 * mm});
        }
    });
